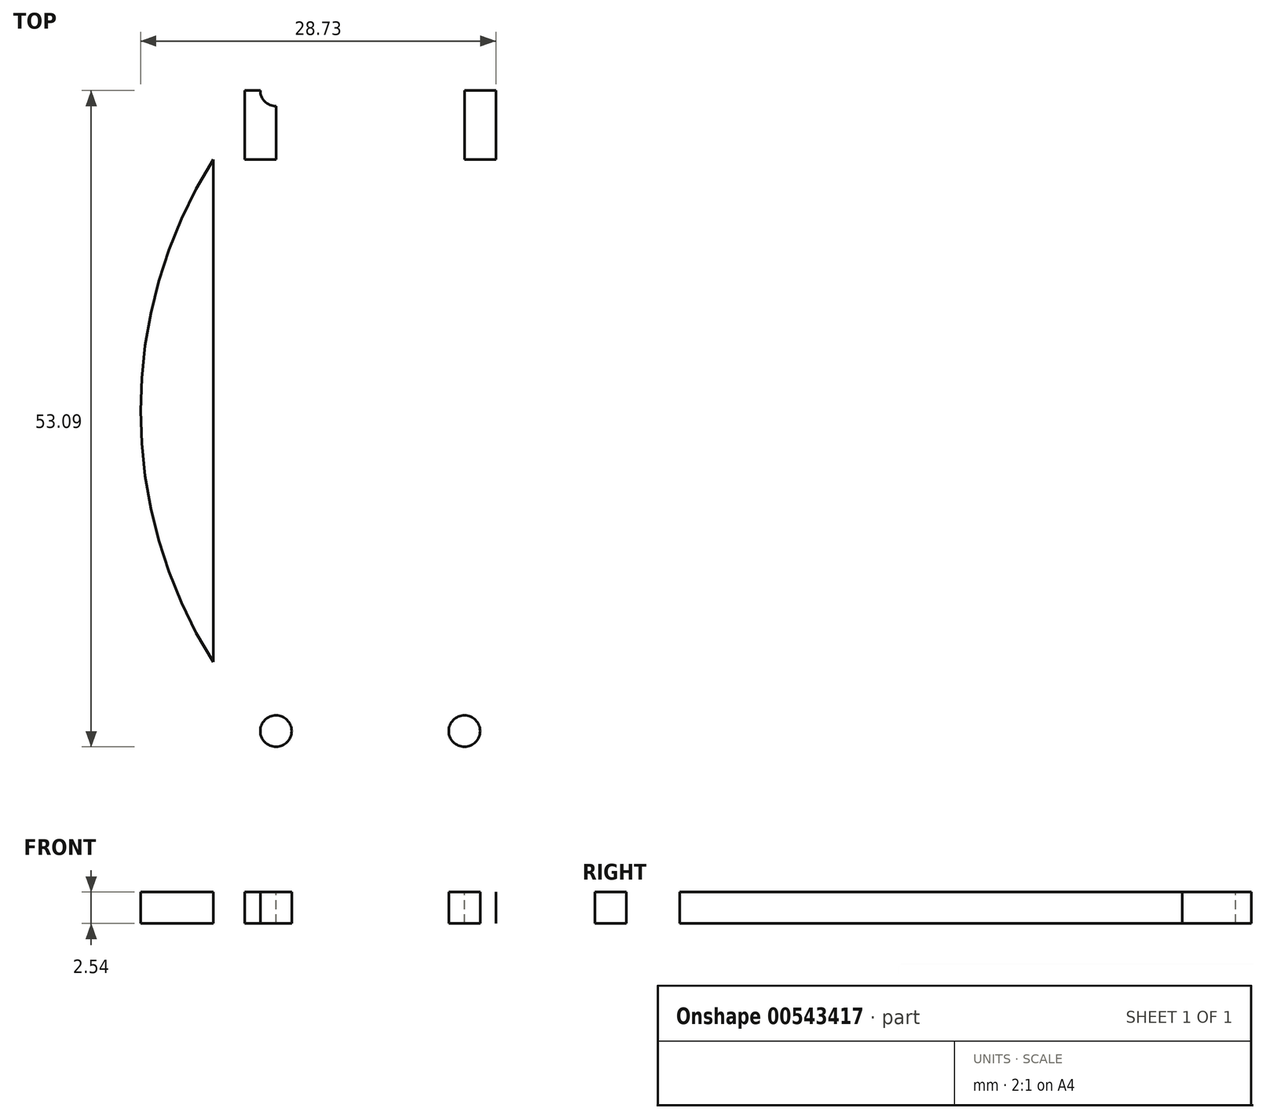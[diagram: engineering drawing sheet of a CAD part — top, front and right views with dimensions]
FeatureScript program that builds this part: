
annotation { "Feature Type Name" : "Feature", "Feature Type Description" : "" }
export const myFeature = defineFeature(function(context is Context, id is Id, definition is map)
    precondition{}
    {
        {
            var Q0;
            Q0=qCreatedBy(makeId("Top.planeOp"),FACE);
            var sketch = newSketch(context, id + "F0", { "sketchPlane" : qUnion([Q0])});
            skLineSegment(sketch, "E0.left", {"start": v(12.7, 50.8) * mm, "end": v(12.7, -50.8) * mm});
            skLineSegment(sketch, "E0.right", {"start": v(-12.7, 50.8) * mm, "end": v(-12.7, -50.8) * mm});
            skPoint(sketch, "E0.middle", {"position": v(0, 0) * mm});
            skLineSegment(sketch, "E1.bottom", {"start": v(6.73, -50.8) * mm, "end": v(-6.73, -50.8) * mm});
            skLineSegment(sketch, "E1.top", {"start": v(6.73, -37.33) * mm, "end": v(-6.73, -37.33) * mm});
            skLineSegment(sketch, "E1.left", {"start": v(6.73, -50.8) * mm, "end": v(6.73, -37.33) * mm});
            skLineSegment(sketch, "E1.right", {"start": v(-6.73, -50.8) * mm, "end": v(-6.73, -37.33) * mm});
            skPoint(sketch, "E1.middle", {"position": v(0, -44.07) * mm});
            skCircle(sketch, "E2", {"center": v(-6.73, -37.33) * mm, "radius": 2.41 * mm});
            skCircle(sketch, "E3", {"center": v(6.73, -37.33) * mm, "radius": 2.41 * mm});
            skCircle(sketch, "E4", {"center": v(6.73, -50.8) * mm, "radius": 2.41 * mm});
            skCircle(sketch, "E5", {"center": v(-6.73, -50.8) * mm, "radius": 2.41 * mm});
            skArc(sketch, "E6", {"start": v(-12.7, -50.8) * mm, "mid": v(0, -63.5) * mm, "end": v(12.7, -50.8) * mm});
            skArc(sketch, "E7", {"start": v(12.7, 50.8) * mm, "mid": v(0, 63.5) * mm, "end": v(-12.7, 50.8) * mm});
            skSolve(sketch);
        }
        {
            var Q0;
            Q0 = qSketchRegion(id + "F0", true);
            var Q1;
            {var subQ5=sQuery(id+"F0.wireOp",EDGE,"E4");var subQ10=sQuery(id+"F0.wireOp",EDGE,"E1.bottom");var subQ15=makeQuery(id+"F0.imprint","INTERSECT",VERTEX,{"derivedFrom":[subQ10,subQ5]});Q1=makeQuery(id+"F0.imprint","IMPRINT",FACE,{"disambiguationData":[TD([[makeQuery(id+"F0.imprint","IMPRINT",EDGE,{"disambiguationData":[TD([[subQ15,-1.0]])],"derivedFrom":subQ10}),-1.0]])]});}
            extrude(context, id + "F1", {"entities" : qUnion([Q0, Q1]), "depth" : 2.54 * mm, "offsetDistance" : 25.4 * mm});
        }
        {
            var Q0;
            Q0=makeQuery(id+"F1.opExtrude","CAP_FACE",FACE,{"disambiguationData":[OSD([sQuery(id+"F0.wireOp",EDGE,"E0.left"),sQuery(id+"F0.wireOp",EDGE,"E0.right"),sQuery(id+"F0.wireOp",EDGE,"E2"),sQuery(id+"F0.wireOp",EDGE,"E3"),sQuery(id+"F0.wireOp",EDGE,"E4"),sQuery(id+"F0.wireOp",EDGE,"E5"),sQuery(id+"F0.wireOp",EDGE,"E6"),sQuery(id+"F0.wireOp",EDGE,"E7")])],"isStart":false});
            var sketch = newSketch(context, id + "F2", { "sketchPlane" : qUnion([Q0])});
            skCircle(sketch, "E8", {"center": v(0, 0) * mm, "radius": 1.46 * mm});
            skSolve(sketch);
        }
        {
            var Q0;
            Q0 = qSketchRegion(id + "F2", true);
            extrude(context, id + "F3", {"entities" : qUnion([Q0]), "operationType" : NewBodyOperationType.REMOVE, "endBound" : BoundingType.THROUGH_ALL, "oppositeDirection" : true, "depth" : 6.35 * mm, "offsetDistance" : 25.4 * mm});
        }
        {
            var Q0;
            Q0=makeQuery(id+"F1.opExtrude","CAP_FACE",FACE,{"disambiguationData":[OSD([sQuery(id+"F0.wireOp",EDGE,"E0.left"),sQuery(id+"F0.wireOp",EDGE,"E0.right"),sQuery(id+"F0.wireOp",EDGE,"E2"),sQuery(id+"F0.wireOp",EDGE,"E3"),sQuery(id+"F0.wireOp",EDGE,"E4"),sQuery(id+"F0.wireOp",EDGE,"E5"),sQuery(id+"F0.wireOp",EDGE,"E6"),sQuery(id+"F0.wireOp",EDGE,"E7")])],"isStart":false});
            var sketch = newSketch(context, id + "F4", { "sketchPlane" : qUnion([Q0])});
            skLineSegment(sketch, "E9.bottom", {"start": v(10.16, 45.05) * mm, "end": v(-10.16, 45.05) * mm});
            skLineSegment(sketch, "E9.top", {"start": v(10.16, 4.41) * mm, "end": v(-10.16, 4.41) * mm});
            skLineSegment(sketch, "E9.left", {"start": v(10.16, 45.05) * mm, "end": v(10.16, 4.41) * mm});
            skLineSegment(sketch, "E9.right", {"start": v(-10.16, 45.05) * mm, "end": v(-10.16, 4.41) * mm});
            skPoint(sketch, "E9.middle", {"position": v(0, 24.73) * mm});
            skLineSegment(sketch, "E10.bottom", {"start": v(-10.16, 45.05) * mm, "end": v(10.16, 45.05) * mm});
            skLineSegment(sketch, "E10.top", {"start": v(-10.16, 50.64) * mm, "end": v(10.16, 50.64) * mm});
            skLineSegment(sketch, "E10.left", {"start": v(-10.16, 45.05) * mm, "end": v(-10.16, 50.64) * mm});
            skLineSegment(sketch, "E10.right", {"start": v(10.16, 45.05) * mm, "end": v(10.16, 50.64) * mm});
            skLineSegment(sketch, "E11", {"start": v(-7.62, 50.64) * mm, "end": v(-7.62, 45.05) * mm});
            skCircle(sketch, "E12", {"center": v(-7.62, 50.64) * mm, "radius": 1.27 * mm});
            skArc(sketch, "E13", {"start": v(-12.7, 45.05) * mm, "mid": v(-18.57, 24.73) * mm, "end": v(-12.7, 4.41) * mm});
            skLineSegment(sketch, "E14", {"start": v(0, 24.73) * mm, "end": v(0, 37.58) * mm});
            skArc(sketch, "E15.MirrorCS", {"start": v(12.7, 45.05) * mm, "mid": v(18.57, 24.73) * mm, "end": v(12.7, 4.41) * mm});
            skLineSegment(sketch, "E16", {"start": v(7.62, 50.64) * mm, "end": v(7.62, 45.05) * mm});
            skCircle(sketch, "E17", {"center": v(7.62, 50.64) * mm, "radius": 1.27 * mm});
            skLineSegment(sketch, "E18", {"start": v(-7.62, 50.64) * mm, "end": v(-7.62, 37.18) * mm});
            skLineSegment(sketch, "E19", {"start": v(-7.62, 37.18) * mm, "end": v(7.62, 37.18) * mm});
            skLineSegment(sketch, "E20", {"start": v(7.62, 37.18) * mm, "end": v(7.62, 50.64) * mm});
            skLineSegment(sketch, "E21", {"start": v(-8.65, 24.73) * mm, "end": v(7.78, 24.73) * mm});
            skCircle(sketch, "E22.MirrorC", {"center": v(-7.62, -1.18) * mm, "radius": 1.27 * mm});
            skCircle(sketch, "E23.MirrorC", {"center": v(7.62, -1.18) * mm, "radius": 1.27 * mm});
            skSolve(sketch);
        }
        {
            var Q0;
            {var subQ0=sQuery(id+"F4.wireOp",EDGE,"E15.MirrorCS");Q0=makeQuery(id+"F4.imprint","IMPRINT",FACE,{"disambiguationData":[TD([[makeQuery(id+"F4.imprint","IMPRINT",EDGE,{"derivedFrom":subQ0}),-1.0]])]});}
            var Q1;
            {var subQ0=sQuery(id+"F4.wireOp",EDGE,"E13");Q1=makeQuery(id+"F4.imprint","IMPRINT",FACE,{"disambiguationData":[TD([[makeQuery(id+"F4.imprint","IMPRINT",EDGE,{"derivedFrom":subQ0}),1.0]])]});}
            var Q2;
            Q2=makeQuery(id+"F1.opExtrude","CAP_FACE",FACE,{"disambiguationData":[OSD([sQuery(id+"F0.wireOp",EDGE,"E0.left"),sQuery(id+"F0.wireOp",EDGE,"E0.right"),sQuery(id+"F0.wireOp",EDGE,"E2"),sQuery(id+"F0.wireOp",EDGE,"E3"),sQuery(id+"F0.wireOp",EDGE,"E4"),sQuery(id+"F0.wireOp",EDGE,"E5"),sQuery(id+"F0.wireOp",EDGE,"E6"),sQuery(id+"F0.wireOp",EDGE,"E7")])],"isStart":true});
            extrude(context, id + "F5", {"entities" : qUnion([Q0, Q1]), "operationType" : NewBodyOperationType.ADD, "endBound" : BoundingType.UP_TO_SURFACE, "oppositeDirection" : true, "depth" : 25.4 * mm, "endBoundEntityFace" : qUnion([Q2]), "offsetDistance" : 25.4 * mm});
        }
        {
            var Q0;
            {var subQ0=sQuery(id+"F4.wireOp",EDGE,"E10.top");var subQ1=makeQuery(id+"F4.imprint","INTERSECT",VERTEX,{"derivedFrom":[subQ0,sQuery(id+"F4.wireOp",EDGE,"E11")]});Q0=makeQuery(id+"F4.imprint","IMPRINT",FACE,{"disambiguationData":[TD([[makeQuery(id+"F4.imprint","IMPRINT",EDGE,{"disambiguationData":[TD([[subQ1,1.0]])],"derivedFrom":subQ0}),1.0]])]});}
            var Q1;
            {var subQ0=sQuery(id+"F4.wireOp",EDGE,"E11");var subQ1=sQuery(id+"F4.wireOp",EDGE,"E10.top");var subQ2=makeQuery(id+"F4.imprint","INTERSECT",VERTEX,{"derivedFrom":[subQ1,subQ0]});Q1=makeQuery(id+"F4.imprint","IMPRINT",FACE,{"disambiguationData":[TD([[makeQuery(id+"F4.imprint","IMPRINT",EDGE,{"disambiguationData":[TD([[subQ2,1.0]])],"derivedFrom":subQ1}),-1.0]])]});}
            var Q2;
            {var subQ0=sQuery(id+"F4.wireOp",EDGE,"E12");var subQ1=sQuery(id+"F4.wireOp",EDGE,"E10.top");var subQ2=makeQuery(id+"F4.imprint","INTERSECT",VERTEX,{"disambiguationData":[OD(0.0)],"derivedFrom":[subQ1,subQ0]});Q2=makeQuery(id+"F4.imprint","IMPRINT",FACE,{"disambiguationData":[TD([[makeQuery(id+"F4.imprint","IMPRINT",EDGE,{"disambiguationData":[TD([[subQ2,1.0]])],"derivedFrom":subQ1}),-1.0]])]});}
            var Q3;
            {var subQ0=sQuery(id+"F4.wireOp",EDGE,"E10.top");var subQ1=makeQuery(id+"F4.imprint","INTERSECT",VERTEX,{"derivedFrom":[subQ0,sQuery(id+"F4.wireOp",EDGE,"E16")]});Q3=makeQuery(id+"F4.imprint","IMPRINT",FACE,{"disambiguationData":[TD([[makeQuery(id+"F4.imprint","IMPRINT",EDGE,{"disambiguationData":[TD([[subQ1,1.0]])],"derivedFrom":subQ0}),1.0]])]});}
            var Q4;
            {var subQ0=sQuery(id+"F4.wireOp",EDGE,"E16");var subQ1=sQuery(id+"F4.wireOp",EDGE,"E10.top");var subQ2=makeQuery(id+"F4.imprint","INTERSECT",VERTEX,{"derivedFrom":[subQ1,subQ0]});Q4=makeQuery(id+"F4.imprint","IMPRINT",FACE,{"disambiguationData":[TD([[makeQuery(id+"F4.imprint","IMPRINT",EDGE,{"disambiguationData":[TD([[subQ2,1.0]])],"derivedFrom":subQ1}),-1.0]])]});}
            var Q5;
            {var subQ0=sQuery(id+"F4.wireOp",EDGE,"E17");var subQ1=sQuery(id+"F4.wireOp",EDGE,"E10.top");var subQ2=makeQuery(id+"F4.imprint","INTERSECT",VERTEX,{"disambiguationData":[OD(0.0)],"derivedFrom":[subQ1,subQ0]});Q5=makeQuery(id+"F4.imprint","IMPRINT",FACE,{"disambiguationData":[TD([[makeQuery(id+"F4.imprint","IMPRINT",EDGE,{"disambiguationData":[TD([[subQ2,1.0]])],"derivedFrom":subQ1}),-1.0]])]});}
            var Q6;
            Q6=makeQuery(id+"F4.imprint","IMPRINT",FACE,{"disambiguationData":[TD([[makeQuery(id+"F4.imprint","IMPRINT",EDGE,{"derivedFrom":sQuery(id+"F4.wireOp",EDGE,"E22.MirrorC")}),-1.0]])]});
            var Q7;
            Q7=makeQuery(id+"F4.imprint","IMPRINT",FACE,{"disambiguationData":[TD([[makeQuery(id+"F4.imprint","IMPRINT",EDGE,{"derivedFrom":sQuery(id+"F4.wireOp",EDGE,"E23.MirrorC")}),-1.0]])]});
            var Q8;
            Q8=makeQuery(id+"F4.imprint","IMPRINT",FACE,{"disambiguationData":[TD([[makeQuery(id+"F4.imprint","IMPRINT",EDGE,{"derivedFrom":sQuery(id+"F4.wireOp",EDGE,"E9.top")}),-1.0]])]});
            var Q9;
            {var subQ3=sQuery(id+"F4.wireOp",EDGE,"E18");Q9=makeQuery(id+"F4.imprint","IMPRINT",FACE,{"disambiguationData":[TD([[makeQuery(id+"F4.imprint","IMPRINT",EDGE,{"derivedFrom":subQ3}),1.0]])]});}
            extrude(context, id + "F6", {"entities" : qUnion([Q0, Q1, Q2, Q3, Q4, Q5, Q6, Q7, Q8, Q9]), "operationType" : NewBodyOperationType.REMOVE, "oppositeDirection" : true, "depth" : 25.4 * mm, "offsetDistance" : 25.4 * mm});
        }
    });
